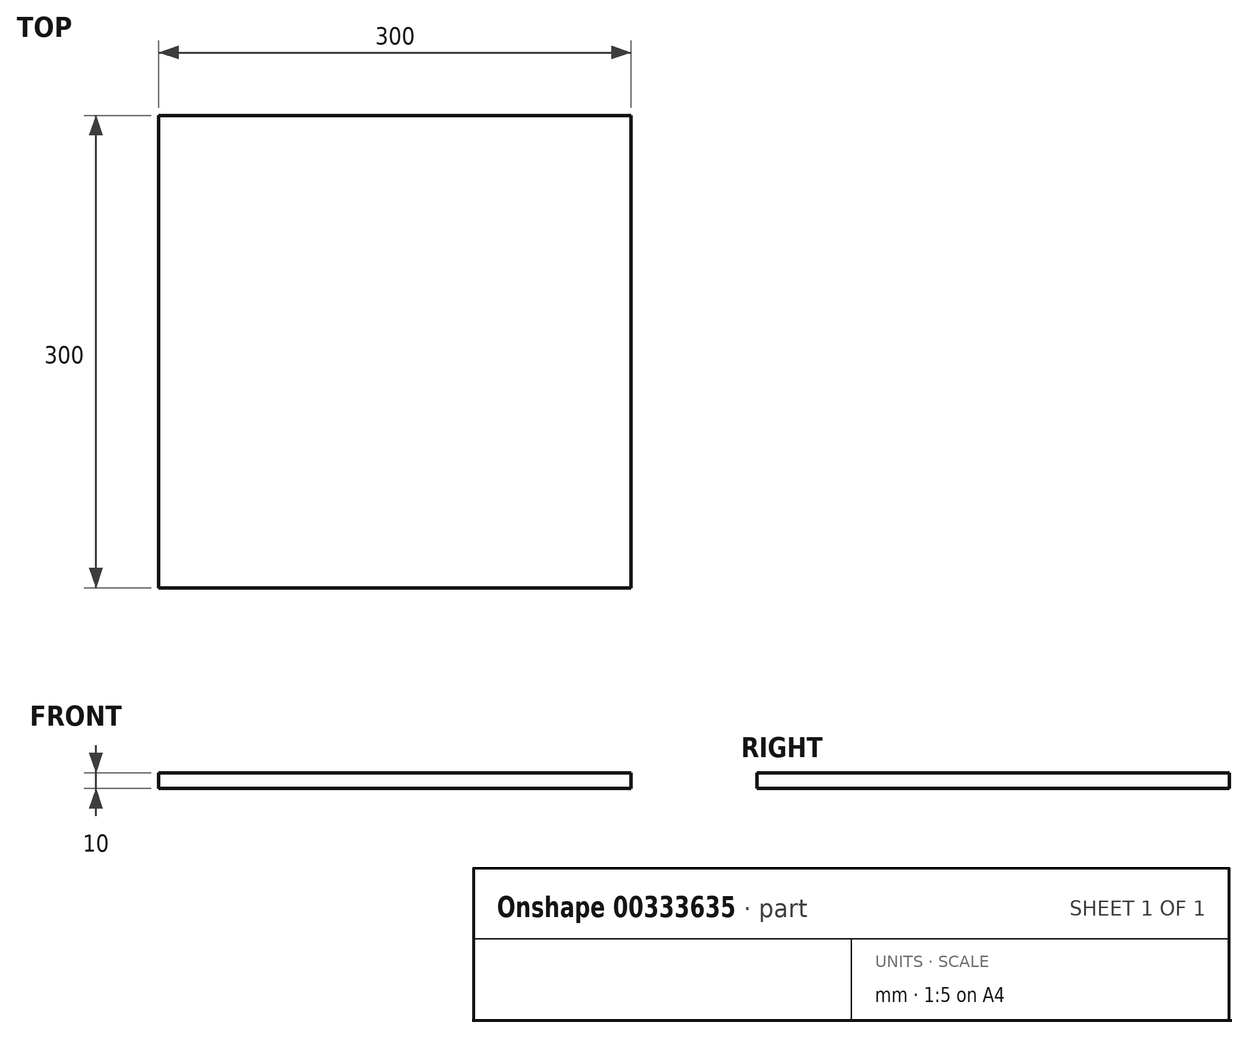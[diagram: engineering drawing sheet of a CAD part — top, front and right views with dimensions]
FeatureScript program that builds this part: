
annotation { "Feature Type Name" : "Feature", "Feature Type Description" : "" }
export const myFeature = defineFeature(function(context is Context, id is Id, definition is map)
    precondition{}
    {
        {
            var Q0;
            Q0=qCreatedBy(makeId("Top.planeOp"),FACE);
            var sketch = newSketch(context, id + "F0", { "sketchPlane" : qUnion([Q0])});
            skLineSegment(sketch, "E0.bottom", {"start": v(0, 0) * mm, "end": v(300, 0) * mm});
            skLineSegment(sketch, "E0.top", {"start": v(0, 300) * mm, "end": v(300, 300) * mm});
            skLineSegment(sketch, "E0.left", {"start": v(0, 0) * mm, "end": v(0, 300) * mm});
            skLineSegment(sketch, "E0.right", {"start": v(300, 0) * mm, "end": v(300, 300) * mm});
            skSolve(sketch);
        }
        {
            var Q0;
            Q0 = qSketchRegion(id + "F0", true);
            extrude(context, id + "F1", {"entities" : qUnion([Q0]), "depth" : 10 * mm});
        }
    });
